# Revit family: Faucet-Deck_Mount-Bath_Shower-KOHLER-STANCE-K-76696T_1
name_source: partatom
category: Plumbing Fixtures
units: mm (PartAtom-declared; Revit-internal decimal feet)

## family parameters
Cut with Voids When Loaded = No
Host = Face
OmniClass Number = 23.31.11.00
OmniClass Title = Faucets
Part Type = Normal
Room Calculation Point = No
Round Connector Dimension = Use Diameter
Shared = No

## types (4) — shared parameters
ADA Compliant = No
Assembly Code = D2010
CW Connection = Yes
Cold Water Inlet = Cold Water Inlet
Date Modified = 11/30/2022
Default Elevation = 36"
Drain Included = No
Flow Rate = 3 GPM
HW Connection = Yes
Handle Clearance = 3 7/16"
Height = 9 11/16"
Hot Water Inlet = Hot Water Inlet
Length = 7 1/4"
Manufacturer = Kohler Co.
Master Format 2014 = 22 41 39
Master Format 2014 Name = Residential Faucets, Supplies, and Trim
Material = Premium Metal Construction
Pressure = 80.00 psi
Product Name = Stance
Spout Reach = 7 1/4"
URL = http://www.kohler.com.cn
Vent Connection = No
Waste Connection = No
Waste Water Outlet = Waste Water Outlet
WaterSense Certified = No
Width = 2 5/16"

## per-type parameters (varying)
| type | 4 | B4 | Description | Finish | Model | Product Documentation Link | Product Page URL | Type |
| B4, 2BL-Black | No | Yes | Three-Hole Cylinder Side Bathtub Shower Faucet (Smart Type) | KOHLER-Metal-2BL-Black | K-76696T-B4-2BL | https://files.kohler.com.cn | https://www.kohler.com.cn | 1 |
| B4, BL-Matte Black | No | Yes | Three-Hole Cylinder Side Bathtub Shower Faucet (Smart Type) | Kohler-Metal-BL-Matte_Black | K-76696T-B4-BL | https://files.kohler.com.cn |  | 2 |
| B4, CP-Polished Chrome | No | Yes | Three-Hole Cylinder Side Bathtub Shower Faucet (Smart Type) | Kohler-Metal-CP-Polished_Chrome | K-76696T-B4-CP | https://files.kohler.com.cn | https://www.kohler.com.cn | 3 |
| 4, BL-Matte Black | Yes | No | 3 Hole Deck Mount Bath Faucet With Hand Shower | Kohler-Metal-BL-Matte_Black | K-76696T-4-BL |  |  | 4 |

## geometry (parser evidence)
native form markers: Sweep x8
no freeform markers — native parametric forms only
